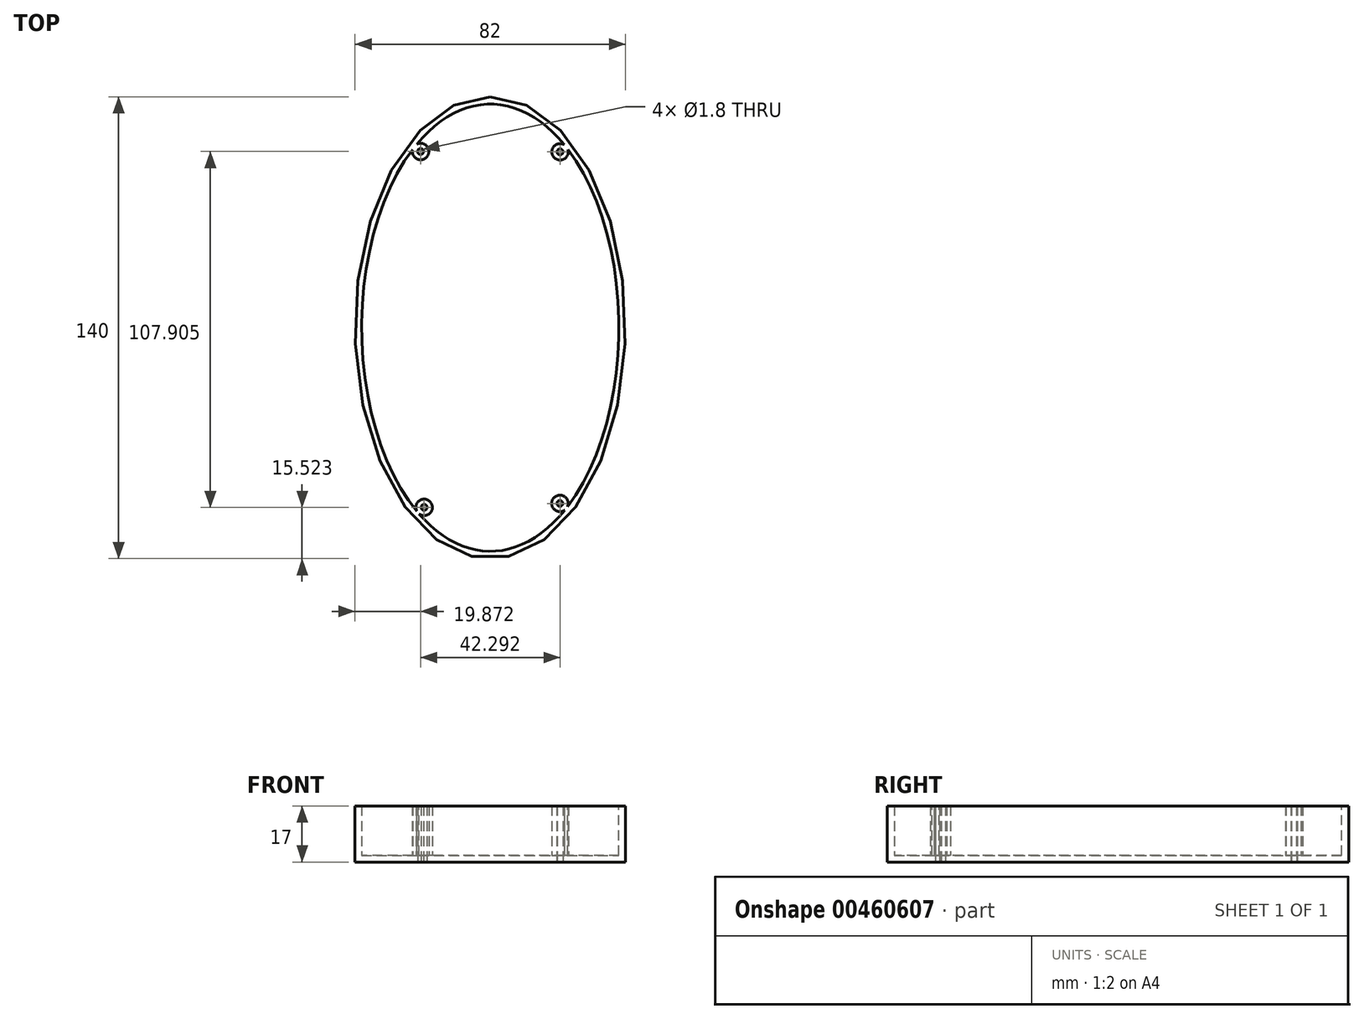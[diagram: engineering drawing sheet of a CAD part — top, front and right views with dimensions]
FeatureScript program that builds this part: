
annotation { "Feature Type Name" : "Feature", "Feature Type Description" : "" }
export const myFeature = defineFeature(function(context is Context, id is Id, definition is map)
    precondition{}
    {
        {
            var Q0;
            Q0=qCreatedBy(makeId("Top.planeOp"),FACE);
            var sketch = newSketch(context, id + "F0", { "sketchPlane" : qUnion([Q0])});
            skEllipse(sketch, "E0", {"center": v(-6.22, 3.26) * mm, "majorRadius": 70 * mm, "minorRadius": 41 * mm, "majorAxis": v(0, 1)});
            skSolve(sketch);
        }
        {
            var Q0;
            Q0=qSketchRegion(id+"F0",true);
            extrude(context, id + "F1", {"entities" : qUnion([Q0]), "depth" : 17 * mm});
        }
        {
            var Q0;
            Q0=makeQuery(id+"F1.opExtrude","CAP_FACE",FACE,{"disambiguationData":[OSD([sQuery(id+"F0.wireOp",EDGE,"E0")])],"isStart":false});
            var sketch = newSketch(context, id + "F2", { "sketchPlane" : qUnion([Q0])});
            skEllipse(sketch, "E1", {"center": v(-6.22, 3.26) * mm, "majorRadius": 67.8 * mm, "minorRadius": 39 * mm, "majorAxis": v(0, 1)});
            skSolve(sketch);
        }
        {
            var Q0;
            Q0=makeQuery(id+"F2.imprint","IMPRINT",FACE,{"disambiguationData":[TD([[makeQuery(id+"F2.imprint","IMPRINT",EDGE,{"derivedFrom":sQuery(id+"F2.wireOp",EDGE,"E1")}),1.0]])]});
            extrude(context, id + "F3", {"entities" : qUnion([Q0]), "operationType" : NewBodyOperationType.REMOVE, "oppositeDirection" : true, "depth" : 15 * mm});
        }
        {
            var Q0;
            Q0=makeQuery(id+"F3.boolean.opBoolean","COPY",FACE,{"derivedFrom":makeQuery(id+"F3.opExtrude","CAP_FACE",FACE,{"disambiguationData":[OSD([sQuery(id+"F2.wireOp",EDGE,"E1")])],"isStart":false})});
            var sketch = newSketch(context, id + "F4", { "sketchPlane" : qUnion([Q0])});
            skCircle(sketch, "E2", {"center": v(-27.35, 56.69) * mm, "radius": 2.5 * mm});
            skPoint(sketch, "E2.first.point", {"position": v(-28.49, 58.91) * mm});
            skPoint(sketch, "E2.second.point", {"position": v(-26.1, 54.53) * mm});
            skPoint(sketch, "E2.third.point", {"position": v(-27.44, 54.19) * mm});
            skCircle(sketch, "E3", {"center": v(-27.35, 56.69) * mm, "radius": 0.9 * mm});
            skSolve(sketch);
        }
        {
            var Q0;
            {var subQ0=sQuery(id+"F4.wireOp",EDGE,"E2");var subQ1=makeQuery(id+"F3.boolean.opBoolean","COPY",EDGE,{"derivedFrom":makeQuery(id+"F3.opExtrude","CAP_EDGE",EDGE,{"disambiguationData":[OSD([sQuery(id+"F2.wireOp",EDGE,"E1")])],"isStart":false})});var subQ2=makeQuery(id+"F4.imprint","INTERSECT",VERTEX,{"disambiguationData":[OD(0.0)],"derivedFrom":[subQ1,subQ0]});Q0=makeQuery(id+"F4.imprint","IMPRINT",FACE,{"disambiguationData":[TD([[makeQuery(id+"F4.imprint","IMPRINT",EDGE,{"disambiguationData":[TD([[subQ2,-1.0]])],"derivedFrom":subQ0}),1.0]])]});}
            extrude(context, id + "F5", {"entities" : qUnion([Q0]), "operationType" : NewBodyOperationType.ADD, "depth" : 15 * mm});
        }
        {
            var Q0;
            Q0=makeQuery(id+"F3.boolean.opBoolean","COPY",FACE,{"derivedFrom":makeQuery(id+"F3.opExtrude","CAP_FACE",FACE,{"disambiguationData":[OSD([sQuery(id+"F2.wireOp",EDGE,"E1")])],"isStart":false})});
            var sketch = newSketch(context, id + "F6", { "sketchPlane" : qUnion([Q0])});
            skCircle(sketch, "E4", {"center": v(14.94, 56.58) * mm, "radius": 2.5 * mm});
            skPoint(sketch, "E4.first.point", {"position": v(12.51, 56) * mm});
            skPoint(sketch, "E4.second.point", {"position": v(17.34, 57.29) * mm});
            skPoint(sketch, "E4.third.point", {"position": v(16.01, 54.32) * mm});
            skCircle(sketch, "E5", {"center": v(14.94, 56.58) * mm, "radius": 0.9 * mm});
            skSolve(sketch);
        }
        {
            var Q0;
            {var subQ0=sQuery(id+"F6.wireOp",EDGE,"E4");var subQ1=makeQuery(id+"F3.boolean.opBoolean","COPY",EDGE,{"derivedFrom":makeQuery(id+"F3.opExtrude","CAP_EDGE",EDGE,{"disambiguationData":[OSD([sQuery(id+"F2.wireOp",EDGE,"E1")])],"isStart":false})});var subQ2=makeQuery(id+"F6.imprint","INTERSECT",VERTEX,{"disambiguationData":[OD(0.0)],"derivedFrom":[subQ1,subQ0]});Q0=makeQuery(id+"F6.imprint","IMPRINT",FACE,{"disambiguationData":[TD([[makeQuery(id+"F6.imprint","IMPRINT",EDGE,{"disambiguationData":[TD([[subQ2,1.0]])],"derivedFrom":subQ0}),1.0]])]});}
            extrude(context, id + "F7", {"entities" : qUnion([Q0]), "operationType" : NewBodyOperationType.ADD, "depth" : 15 * mm});
        }
        {
            var Q0;
            Q0=makeQuery(id+"F3.boolean.opBoolean","COPY",FACE,{"derivedFrom":makeQuery(id+"F3.opExtrude","CAP_FACE",FACE,{"disambiguationData":[OSD([sQuery(id+"F2.wireOp",EDGE,"E1")])],"isStart":false})});
            var sketch = newSketch(context, id + "F8", { "sketchPlane" : qUnion([Q0])});
            skCircle(sketch, "E6", {"center": v(-26.28, -51.22) * mm, "radius": 2.5 * mm});
            skPoint(sketch, "E6.first.point", {"position": v(-28.49, -50.03) * mm});
            skPoint(sketch, "E6.second.point", {"position": v(-24.98, -49.08) * mm});
            skPoint(sketch, "E6.third.point", {"position": v(-28.49, -52.4) * mm});
            skCircle(sketch, "E7", {"center": v(-26.28, -51.22) * mm, "radius": 0.9 * mm});
            skSolve(sketch);
        }
        {
            var Q0;
            {var subQ0=sQuery(id+"F8.wireOp",EDGE,"E6");var subQ1=makeQuery(id+"F7.boolean.opBoolean","SPLIT",EDGE,{"disambiguationData":[OD(0.0)],"derivedFrom":makeQuery(id+"F3.boolean.opBoolean","COPY",EDGE,{"derivedFrom":makeQuery(id+"F3.opExtrude","CAP_EDGE",EDGE,{"disambiguationData":[OSD([sQuery(id+"F2.wireOp",EDGE,"E1")])],"isStart":false})})});var subQ2=makeQuery(id+"F8.imprint","INTERSECT",VERTEX,{"disambiguationData":[OD(0.0)],"derivedFrom":[subQ1,subQ0]});Q0=makeQuery(id+"F8.imprint","IMPRINT",FACE,{"disambiguationData":[TD([[makeQuery(id+"F8.imprint","IMPRINT",EDGE,{"disambiguationData":[TD([[subQ2,1.0]])],"derivedFrom":subQ0}),1.0]])]});}
            extrude(context, id + "F9", {"entities" : qUnion([Q0]), "operationType" : NewBodyOperationType.ADD, "depth" : 15 * mm});
        }
        {
            var Q0;
            Q0=makeQuery(id+"F3.boolean.opBoolean","COPY",FACE,{"derivedFrom":makeQuery(id+"F3.opExtrude","CAP_FACE",FACE,{"disambiguationData":[OSD([sQuery(id+"F2.wireOp",EDGE,"E1")])],"isStart":false})});
            var sketch = newSketch(context, id + "F10", { "sketchPlane" : qUnion([Q0])});
            skCircle(sketch, "E8", {"center": v(14.89, -50.02) * mm, "radius": 2.5 * mm});
            skPoint(sketch, "E8.first.point", {"position": v(17.2, -50.95) * mm});
            skPoint(sketch, "E8.second.point", {"position": v(12.45, -49.45) * mm});
            skPoint(sketch, "E8.third.point", {"position": v(13.95, -47.7) * mm});
            skCircle(sketch, "E9", {"center": v(14.89, -50.02) * mm, "radius": 0.9 * mm});
            skSolve(sketch);
        }
        {
            var Q0;
            {var subQ0=sQuery(id+"F10.wireOp",EDGE,"E8");var subQ1=sQuery(id+"F2.wireOp",EDGE,"E1");var subQ2=makeQuery(id+"F9.boolean.opBoolean","SPLIT",EDGE,{"disambiguationData":[TD([makeQuery(id+"F7.opExtrude","SWEPT_FACE",FACE,{"disambiguationData":[OSD([sQuery(id+"F6.wireOp",EDGE,"E4")])]})])],"derivedFrom":makeQuery(id+"F7.boolean.opBoolean","SPLIT",EDGE,{"disambiguationData":[OD(0.0)],"derivedFrom":makeQuery(id+"F3.boolean.opBoolean","COPY",EDGE,{"derivedFrom":makeQuery(id+"F3.opExtrude","CAP_EDGE",EDGE,{"disambiguationData":[OSD([subQ1])],"isStart":false})})})});var subQ3=makeQuery(id+"F10.imprint","INTERSECT",VERTEX,{"disambiguationData":[OD(0.0)],"derivedFrom":[subQ2,subQ0]});Q0=makeQuery(id+"F10.imprint","IMPRINT",FACE,{"disambiguationData":[TD([[makeQuery(id+"F10.imprint","IMPRINT",EDGE,{"disambiguationData":[TD([[subQ3,-1.0]])],"derivedFrom":subQ0}),1.0]])]});}
            extrude(context, id + "F11", {"entities" : qUnion([Q0]), "operationType" : NewBodyOperationType.ADD, "depth" : 15 * mm});
        }
        {
            var Q0;
            {var subQ0=sQuery(id+"F2.wireOp",EDGE,"E1");Q0=makeQuery(id+"F11.boolean.opBoolean","MERGE",FACE,{"derivedFrom":[makeQuery(id+"F9.boolean.opBoolean","MERGE",FACE,{"derivedFrom":[makeQuery(id+"F7.boolean.opBoolean","MERGE",FACE,{"derivedFrom":[makeQuery(id+"F5.boolean.opBoolean","MERGE",FACE,{"derivedFrom":[makeQuery(id+"F1.opExtrude","CAP_FACE",FACE,{"disambiguationData":[OSD([sQuery(id+"F0.wireOp",EDGE,"E0")])],"isStart":false}),makeQuery(id+"F5.opExtrude","CAP_FACE",FACE,{"disambiguationData":[OSD([subQ0,sQuery(id+"F4.wireOp",EDGE,"E2")])],"isStart":false})]}),makeQuery(id+"F7.opExtrude","CAP_FACE",FACE,{"disambiguationData":[OSD([subQ0,sQuery(id+"F6.wireOp",EDGE,"E4")])],"isStart":false})]}),makeQuery(id+"F9.opExtrude","CAP_FACE",FACE,{"disambiguationData":[OSD([subQ0,sQuery(id+"F8.wireOp",EDGE,"E6")])],"isStart":false})]}),makeQuery(id+"F11.opExtrude","CAP_FACE",FACE,{"disambiguationData":[OSD([subQ0,sQuery(id+"F10.wireOp",EDGE,"E8")])],"isStart":false})]});}
            var sketch = newSketch(context, id + "F12", { "sketchPlane" : qUnion([Q0])});
            skSolve(sketch);
        }
        {
            var Q0;
            {var subQ8=sQuery(id+"F0.wireOp",EDGE,"E0");Q0=makeQuery(id+"F12.imprint","IMPRINT",FACE,{"disambiguationData":[TD([[makeQuery(id+"F12.imprint","IMPRINT",EDGE,{"derivedFrom":makeQuery(id+"F1.opExtrude","CAP_EDGE",EDGE,{"disambiguationData":[OSD([subQ8])],"isStart":false})}),1.0]])]});}
            var sketch = newSketch(context, id + "F13", { "sketchPlane" : qUnion([Q0])});
            skCircle(sketch, "E10.0", {"center": v(-27.35, 56.69) * mm, "radius": 0.9 * mm});
            skCircle(sketch, "E11.0", {"center": v(14.94, 56.58) * mm, "radius": 0.9 * mm});
            skCircle(sketch, "E12.0", {"center": v(-26.28, -51.22) * mm, "radius": 0.9 * mm});
            skCircle(sketch, "E13.0", {"center": v(14.89, -50.02) * mm, "radius": 0.9 * mm});
            skSolve(sketch);
        }
        {
            var Q0;
            Q0=qSketchRegion(id+"F13",true);
            extrude(context, id + "F14", {"entities" : qUnion([Q0]), "operationType" : NewBodyOperationType.REMOVE, "endBound" : BoundingType.THROUGH_ALL, "oppositeDirection" : true, "depth" : 25 * mm});
        }
    });
